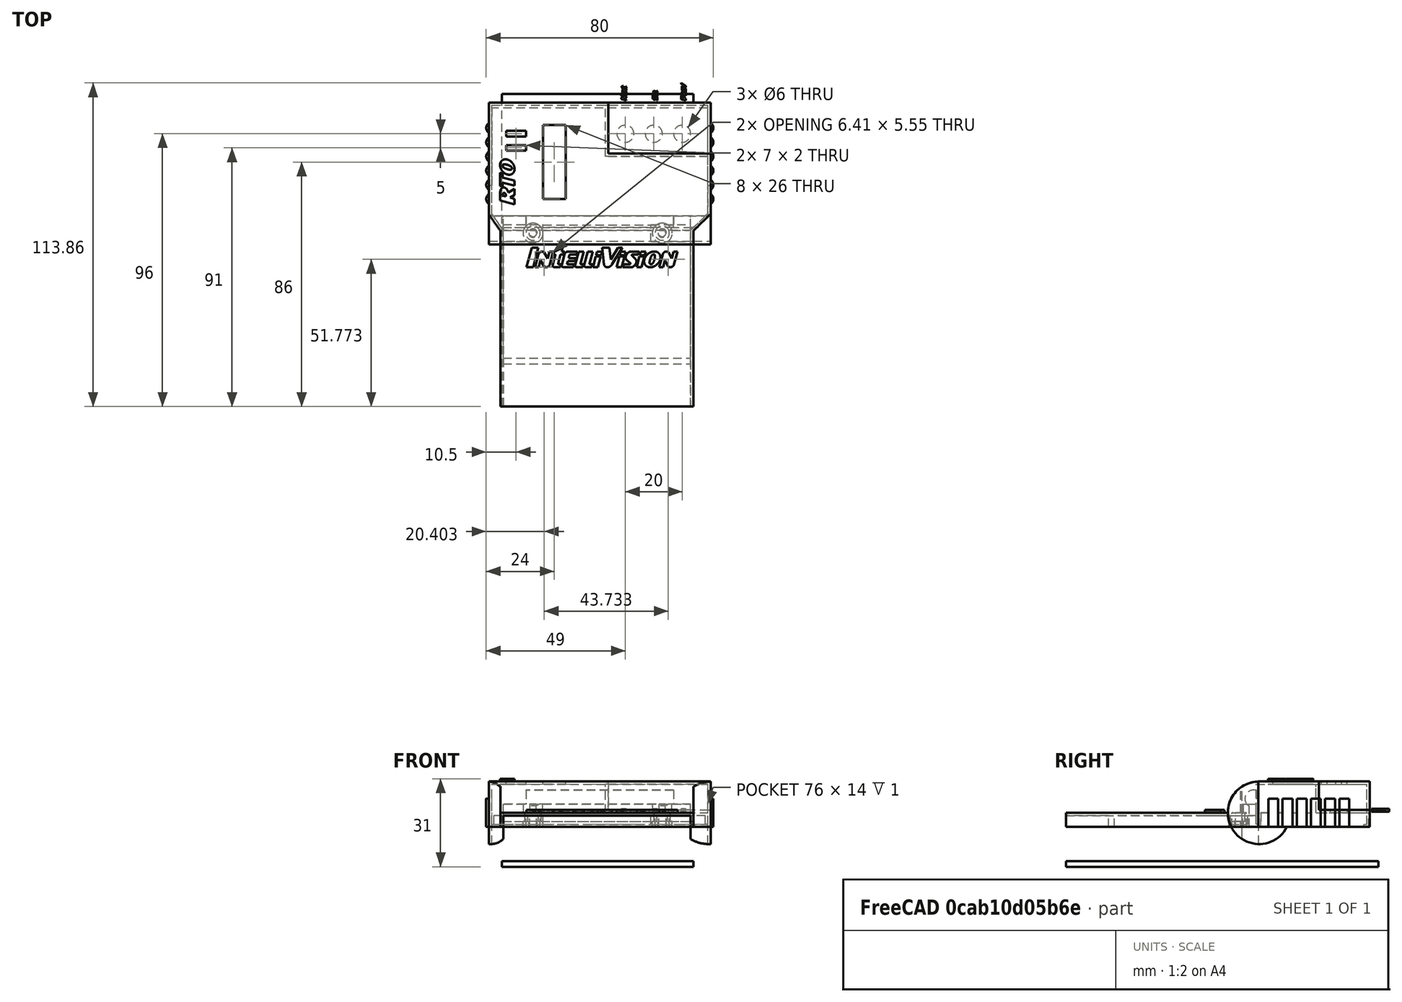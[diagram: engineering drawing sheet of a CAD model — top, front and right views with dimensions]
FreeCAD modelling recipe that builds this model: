
FCSTD DOCUMENT  (FreeCAD 0.20R29410 (Git))
Label: RTO11a_Cart_TOP
License: All rights reserved
LicenseURL: http://en.wikipedia.org/wiki/All_rights_reserved
objects: Part::Box×20, Part::Cut×19, Part::MultiFuse×18, Part::Cylinder×17, Part::Extrusion×6, Part::Part2DObjectPython×5, Part::FeaturePython×4, Part::Feature×4, Sketcher::SketchObject×3, PartDesign::Body×3, PartDesign::Pad×2, Part::Fillet×2, Mesh::Feature×2
note: 105 computed .brp shape members not serialized (recipe doc carries the construction recipe); baked Part::Feature solids carry a one-line shape summary decoded from their .brp

FEATURE [Sketcher::SketchObject] Sketch
  FullyConstrained = true
  MapMode = 5
  Support = -> [XY_Plane009]
  sketch-geometry (4):
    g0: LineSegment StartX=-67.5 StartY=110 StartZ=0 EndX=0 EndY=110 EndZ=0
    g1: LineSegment StartX=0 StartY=110 StartZ=0 EndX=0 EndY=0 EndZ=0
    g2: LineSegment StartX=0 StartY=0 StartZ=0 EndX=-67.5 EndY=0 EndZ=0
    g3: LineSegment StartX=-67.5 StartY=0 StartZ=0 EndX=-67.5 EndY=110 EndZ=0
  constraints (12):
    c: Coincident(g0,g1)
    c: Coincident(g1,g2)
    c: Coincident(g2,g3)
    c: Coincident(g3,g0)
    c: Horizontal(g0)
    c: Horizontal(g2)
    c: Vertical(g1)
    c: Vertical(g3)
    c: DistanceX(g0,g0) = 67.5
    c: DistanceY(g1,g1) = 110
    c: DistanceX(g-1,g1) = 0
    c: DistanceY(g1,g-1) = 0
FEATURE [PartDesign::Pad] Pad
  Direction = (0,0,1)
  Length = 2
  Length2 = 10
  Profile = -> Sketch
  ReferenceAxis = -> Sketch [N_Axis]
  Type = 0
FEATURE [PartDesign::Body] Body002  label="TOP"
  Origin = -> Origin002
  Placement = pos=(0,0,4) rot=(0,0,1;0rad)
FEATURE [PartDesign::Body] Body
  Group = -> [Sketch,Pad]
  Origin = -> Origin007
  Tip = -> Pad
FEATURE [Part::FeaturePython] Tube  # WARN: FeaturePython — macro-defined, semantics opaque (R4)
  AttacherType = Attacher::AttachEngine3D
  Height = 5
  InnerRadius = 1.25
  OuterRadius = 2.5
  Placement = pos=(-11,61,14) rot=(0,0,1;0rad)
FEATURE [Part::FeaturePython] Tube001  # WARN: FeaturePython — macro-defined, semantics opaque (R4)
  AttacherType = Attacher::AttachEngine3D
  Height = 5
  InnerRadius = 1.25
  OuterRadius = 2.5
  Placement = pos=(-56.5,61,14) rot=(0,0,1;0rad)
FEATURE [Part::Part2DObjectPython] ShapeString  # Draft 2D object (typed FeaturePython)
  FontFile = <userpath>/Documents/Retrocomputer/Intellivision/3DModel/sfintell.ttf
  MakeFace = true
  Size = 4
  String = IntelliVision
  Tracking = 0
FEATURE [Part::Extrusion] Extrude  label="Scritta"
  Base = -> ShapeString
  Dir = (0,0,1)
  DirMode = 2
  FaceMakerClass = Part::FaceMakerBullseye
  LengthFwd = 2
  LengthRev = 0
  Placement = pos=(-59,49,18) rot=(0,0,1;0rad)
  Solid = false
  Symmetric = false
FEATURE [Part::Box] Box  label="BasePillarSx"
  AttacherType = Attacher::AttachEngine3D
  Height = 3
  Length = 14
  Placement = pos=(-67,58,15) rot=(0,0,1;0rad)
  Width = 6
FEATURE [Part::Box] Box006  label="BasePillarDx"
  AttacherType = Attacher::AttachEngine3D
  Height = 3
  Length = 14
  Placement = pos=(-15,58,15) rot=(0,0,1;0rad)
  Width = 6
FEATURE [Sketcher::SketchObject] Sketch022
  AttachmentOffset = pos=(0,0,19) rot=(0,0,1;0rad)
  FullyConstrained = true
  MapMode = 5
  Placement = pos=(0,0,19) rot=(0,0,1;0rad)
  Support = -> [XY_Plane]
  sketch-geometry (8):
    g0: LineSegment StartX=0 StartY=0 StartZ=0 EndX=-68 EndY=0 EndZ=0
    g1: LineSegment StartX=-68 StartY=0 StartZ=0 EndX=-68 EndY=62 EndZ=0
    g2: LineSegment StartX=-68 StartY=62 StartZ=0 EndX=-72.0041 EndY=68.6121 EndZ=0
    g3: LineSegment StartX=-72.0041 StartY=68.6121 StartZ=0 EndX=-72.0041 EndY=106.612 EndZ=0
    g4: LineSegment StartX=-72.0041 StartY=106.612 StartZ=0 EndX=5.99595 EndY=106.612 EndZ=0
    g5: LineSegment StartX=5.99595 StartY=106.612 StartZ=0 EndX=5.99595 EndY=69.6121 EndZ=0
    g6: LineSegment StartX=5.99595 StartY=69.6121 StartZ=0 EndX=-9e-16 EndY=62 EndZ=0
    g7: LineSegment StartX=-9e-16 StartY=62 StartZ=0 EndX=0 EndY=0 EndZ=0
  constraints (24):
    c: PointOnObject(g0,g-2)
    c: PointOnObject(g0,g-1)
    c: Horizontal(g0)
    c: Coincident(g0,g1)
    c: Vertical(g1)
    c: Coincident(g1,g2)
    c: Coincident(g2,g3)
    c: Vertical(g3)
    c: Coincident(g3,g4)
    c: Horizontal(g4)
    c: Coincident(g4,g5)
    c: Vertical(g5)
    c: Coincident(g5,g6)
    c: PointOnObject(g6,g-2)
    c: Coincident(g6,g7)
    c: DistanceY(g1,g1) = 62
    c: DistanceY(g7,g7) = 62
    c: Coincident(g0,g7)
    c: DistanceX(g4,g4) = 78
    c: DistanceX(g0,g0) = 68
    c: DistanceY(g3,g3) = 38
    c: DistanceY(g5,g5) = 37
    c: Distance(g6) = 9.69
    c: Distance(g2) = 7.73
FEATURE [Part::Extrusion] Extrude001  label="BaseEsterna"
  Base = -> Sketch022
  Dir = (0,0,1)
  DirMode = 2
  FaceMakerClass = Part::FaceMakerBullseye
  LengthFwd = 5
  LengthRev = 0
  Reversed = true
  Solid = true
  Symmetric = false
FEATURE [Sketcher::SketchObject] Sketch005
  AttachmentOffset = pos=(-1,0,3) rot=(0,0,1;0rad)
  FullyConstrained = true
  MapMode = 5
  Placement = pos=(-1,0,3) rot=(0,0,1;0rad)
  Support = -> [XY_Plane010]
  sketch-geometry (8):
    g0: LineSegment StartX=0 StartY=0 StartZ=0 EndX=-66 EndY=0 EndZ=0
    g1: LineSegment StartX=-66 StartY=0 StartZ=0 EndX=-66 EndY=62 EndZ=0
    g2: LineSegment StartX=-66 StartY=62 StartZ=0 EndX=-70 EndY=67.82 EndZ=0
    g3: LineSegment StartX=-70 StartY=67.82 StartZ=0 EndX=-70 EndY=105 EndZ=0
    g4: LineSegment StartX=-70 StartY=105 StartZ=0 EndX=6 EndY=105 EndZ=0
    g5: LineSegment StartX=6 StartY=105 StartZ=0 EndX=6 EndY=67.82 EndZ=0
    g6: LineSegment StartX=6 StartY=67.82 StartZ=0 EndX=0 EndY=62 EndZ=0
    g7: LineSegment StartX=0 StartY=62 StartZ=0 EndX=0 EndY=0 EndZ=0
  constraints (24):
    c: PointOnObject(g0,g-2)
    c: PointOnObject(g0,g-1)
    c: Horizontal(g0)
    c: Coincident(g0,g1)
    c: Vertical(g1)
    c: Coincident(g1,g2)
    c: Coincident(g2,g3)
    c: Vertical(g3)
    c: Coincident(g3,g4)
    c: Horizontal(g4)
    c: Coincident(g4,g5)
    c: Vertical(g5)
    c: Coincident(g5,g6)
    c: PointOnObject(g6,g-2)
    c: Coincident(g6,g7)
    c: DistanceY(g1,g1) = 62
    c: DistanceY(g7,g7) = 62
    c: Coincident(g0,g7)
    c: DistanceX(g4,g4) = 76
    c: DistanceX(g0,g0) = 66
    c: Distance(g1,g4) = 43
    c: DistanceX(g2,g1) = 4
    c: DistanceY(g5,g2) = 0
    c: DistanceY(g6,g5) = 5.82
FEATURE [PartDesign::Pad] Pad001
  Direction = (0,0,1)
  Length = 15
  Length2 = 10
  Profile = -> Sketch005
  ReferenceAxis = -> Sketch005 [N_Axis]
  Type = 0
FEATURE [PartDesign::Body] Body003  label="BaseInterna"
  Group = -> [Sketch005,Pad001]
  Origin = -> Origin
  Tip = -> Pad001
FEATURE [Part::Box] Box007  label="Cubo"
  AttacherType = Attacher::AttachEngine3D
  Height = 16
  Length = 78
  Placement = pos=(-72,68,14) rot=(0,0,1;0rad)
  Width = 39
FEATURE [Part::Cylinder] Cylinder  label="Cilindro"
  Angle = 360
  AttacherType = Attacher::AttachEngine3D
  FirstAngle = 0
  Height = 78
  Placement = pos=(6,68,19) rot=(0,-1,0;1.5708rad)
  Radius = 11
  SecondAngle = 0
FEATURE [Part::MultiFuse] Fusion
  Shapes = -> [Extrude001,Box007,Cylinder]
FEATURE [Part::Box] Box008  label="Cubo001"
  AttacherType = Attacher::AttachEngine3D
  Height = 14
  Length = 76
  Placement = pos=(-71,67,15) rot=(0,0,1;0rad)
  Width = 39
FEATURE [Part::Box] Box009  label="Cubo002"
  AttacherType = Attacher::AttachEngine3D
  Height = 10
  Length = 66
  Placement = pos=(-67,62,12) rot=(0,0,1;0rad)
  Width = 6
FEATURE [Part::Cylinder] Cylinder006  label="Cilindro006"
  Angle = 360
  AttacherType = Attacher::AttachEngine3D
  FirstAngle = 0
  Height = 10
  Placement = pos=(5,78,1) rot=(0,0,1;0rad)
  Radius = 2
  SecondAngle = 0
FEATURE [Part::Cylinder] Cylinder007  label="Cilindro007"
  Angle = 360
  AttacherType = Attacher::AttachEngine3D
  FirstAngle = 0
  Height = 10
  Placement = pos=(5,73,1) rot=(0,0,1;0rad)
  Radius = 2
  SecondAngle = 0
FEATURE [Part::Cylinder] Cylinder008  label="Cilindro008"
  Angle = 360
  AttacherType = Attacher::AttachEngine3D
  FirstAngle = 0
  Height = 10
  Placement = pos=(5,83,1) rot=(0,0,1;0rad)
  Radius = 2
  SecondAngle = 0
FEATURE [Part::Cylinder] Cylinder009  label="Cilindro009"
  Angle = 360
  AttacherType = Attacher::AttachEngine3D
  FirstAngle = 0
  Height = 10
  Placement = pos=(5,88,1) rot=(0,0,1;0rad)
  Radius = 2
  SecondAngle = 0
FEATURE [Part::Cylinder] Cylinder010  label="Cilindro010"
  Angle = 360
  AttacherType = Attacher::AttachEngine3D
  FirstAngle = 0
  Height = 10
  Placement = pos=(5,93,1) rot=(0,0,1;0rad)
  Radius = 2
  SecondAngle = 0
FEATURE [Part::Cylinder] Cylinder011  label="Cilindro011"
  Angle = 360
  AttacherType = Attacher::AttachEngine3D
  FirstAngle = 0
  Height = 10
  Placement = pos=(5,98,1) rot=(0,0,1;0rad)
  Radius = 2
  SecondAngle = 0
FEATURE [Part::MultiFuse] Fusion009  label="cil_rx"
  Placement = pos=(0,0,13) rot=(0,0,1;0rad)
  Shapes = -> [Cylinder006,Cylinder007,Cylinder008,Cylinder009,Cylinder010,Cylinder011]
FEATURE [Part::Cylinder] Cylinder012  label="Cilindro012"
  Angle = 360
  AttacherType = Attacher::AttachEngine3D
  FirstAngle = 0
  Height = 10
  Placement = pos=(5,78,1) rot=(0,0,1;0rad)
  Radius = 2
  SecondAngle = 0
FEATURE [Part::Cylinder] Cylinder013  label="Cilindro013"
  Angle = 360
  AttacherType = Attacher::AttachEngine3D
  FirstAngle = 0
  Height = 10
  Placement = pos=(5,73,1) rot=(0,0,1;0rad)
  Radius = 2
  SecondAngle = 0
FEATURE [Part::Cylinder] Cylinder014  label="Cilindro014"
  Angle = 360
  AttacherType = Attacher::AttachEngine3D
  FirstAngle = 0
  Height = 10
  Placement = pos=(5,83,1) rot=(0,0,1;0rad)
  Radius = 2
  SecondAngle = 0
FEATURE [Part::Cylinder] Cylinder015  label="Cilindro015"
  Angle = 360
  AttacherType = Attacher::AttachEngine3D
  FirstAngle = 0
  Height = 10
  Placement = pos=(5,88,1) rot=(0,0,1;0rad)
  Radius = 2
  SecondAngle = 0
FEATURE [Part::Cylinder] Cylinder016  label="Cilindro016"
  Angle = 360
  AttacherType = Attacher::AttachEngine3D
  FirstAngle = 0
  Height = 10
  Placement = pos=(5,93,1) rot=(0,0,1;0rad)
  Radius = 2
  SecondAngle = 0
FEATURE [Part::Cylinder] Cylinder017  label="Cilindro017"
  Angle = 360
  AttacherType = Attacher::AttachEngine3D
  FirstAngle = 0
  Height = 10
  Placement = pos=(5,98,1) rot=(0,0,1;0rad)
  Radius = 2
  SecondAngle = 0
FEATURE [Part::MultiFuse] Fusion010  label="cil_dx"
  Placement = pos=(-76,0,13) rot=(0,0,1;0rad)
  Shapes = -> [Cylinder012,Cylinder013,Cylinder014,Cylinder015,Cylinder016,Cylinder017]
FEATURE [Part::MultiFuse] Fusion011
  Shapes = -> [Fusion,Fusion009,Fusion010]
FEATURE [Part::Cut] Cut
  Base = -> Fusion011
  Tool = -> Body003
FEATURE [Part::Cut] Cut001
  Base = -> Cut
  Tool = -> Box009
FEATURE [Part::Cylinder] Cylinder018  label="Bt3"
  Angle = 360
  AttacherType = Attacher::AttachEngine3D
  FirstAngle = 0
  Height = 10
  Placement = pos=(-4,96,16) rot=(0,0,1;0rad)
  Radius = 3
  SecondAngle = 0
FEATURE [Part::Cylinder] Cylinder019  label="Bt2"
  Angle = 360
  AttacherType = Attacher::AttachEngine3D
  FirstAngle = 0
  Height = 10
  Placement = pos=(-14,96,16) rot=(0,0,1;0rad)
  Radius = 3
  SecondAngle = 0
FEATURE [Part::Cylinder] Cylinder020  label="Bt1"
  Angle = 360
  AttacherType = Attacher::AttachEngine3D
  FirstAngle = 0
  Height = 10
  Placement = pos=(-24,96,16) rot=(0,0,1;0rad)
  Radius = 3
  SecondAngle = 0
FEATURE [Part::Box] Box010  label="Cubo003"
  AttacherType = Attacher::AttachEngine3D
  Height = 10
  Length = 8
  Placement = pos=(-53,73,22) rot=(0,0,1;0rad)
  Width = 26
FEATURE [Part::Box] Box011  label="Cubo004"
  AttacherType = Attacher::AttachEngine3D
  Height = 21
  Length = 11
  Placement = pos=(5,57,10) rot=(0,0,1;0.767945rad)
  Width = 7
FEATURE [Part::Box] Box012  label="Cubo005"
  AttacherType = Attacher::AttachEngine3D
  Height = 22
  Length = 8
  Placement = pos=(-75.7,65.86,10) rot=(0,0,-1;0.959931rad)
  Width = 4
FEATURE [Part::Box] Box013  label="Cubo006"
  AttacherType = Attacher::AttachEngine3D
  Height = 20
  Length = 93
  Placement = pos=(-80,49,-6) rot=(0,0,1;0rad)
  Width = 30
FEATURE [Part::MultiFuse] Fusion012
  Shapes = -> [Extrude]
FEATURE [Part::Part2DObjectPython] ShapeString001  # Draft 2D object (typed FeaturePython)
  FontFile = <userpath>/Documents/Retrocomputer/Intellivision/3DModel/sfintell.ttf
  MakeFace = true
  Placement = pos=(0,0,0) rot=(0,0,1;1.5708rad)
  Size = 3
  String = RTO
  Tracking = 0
FEATURE [Part::Extrusion] Extrude002  label="ScrittaRTO"
  Base = -> ShapeString001
  Dir = (0,0,1)
  DirMode = 2
  FaceMakerClass = Part::FaceMakerBullseye
  LengthFwd = 2
  LengthRev = 0
  Placement = pos=(-63,71,29) rot=(1,0,0;0rad)
  Solid = false
  Symmetric = false
FEATURE [Part::MultiFuse] Fusion013  label="Scritte"
  Shapes = -> [Fusion012,Extrude002]
FEATURE [Part::MultiFuse] Fusion014  label="FinaleTOP"
  Shapes = -> [Fusion013]
FEATURE [Part::Cut] Cut010
  Base = -> Cut001
  Tool = -> Box008
FEATURE [Part::Cut] Cut011
  Base = -> Cut010
  Tool = -> Box013
FEATURE [Part::Box] Box014  label="holdertop"
  AttacherType = Attacher::AttachEngine3D
  Height = 5
  Length = 66
  Placement = pos=(-67,15,14) rot=(0,0,1;0rad)
  Width = 2
FEATURE [Part::MultiFuse] Fusion016
  Shapes = -> [Fusion014]
FEATURE [Part::Box] Box015  label="BtnsPlace"
  AttacherType = Attacher::AttachEngine3D
  Height = 10
  Length = 38
  Placement = pos=(-30,89,20) rot=(0,0,1;0rad)
  Width = 18
FEATURE [Part::Cut] Cut015  label="Scritte001"
  Base = -> Fusion016
  Tool = -> Box015
FEATURE [Part::Box] Box016  label="Cubo009"
  AttacherType = Attacher::AttachEngine3D
  Height = 1
  Length = 35
  Placement = pos=(-30,89,19) rot=(0,0,1;0rad)
  Width = 18
FEATURE [Part::Box] Box017  label="Cubo010"
  AttacherType = Attacher::AttachEngine3D
  Height = 11
  Length = 35
  Placement = pos=(-30,88,19) rot=(0,0,1;0rad)
  Width = 1
FEATURE [Part::Box] Box018  label="Cubo011"
  AttacherType = Attacher::AttachEngine3D
  Height = 11
  Length = 1
  Placement = pos=(-31,88,19) rot=(0,0,1;0rad)
  Width = 18
FEATURE [Part::Box] Box019  label="Cubo012"
  AttacherType = Attacher::AttachEngine3D
  Height = 1
  Length = 1
  Placement = pos=(4,88,19) rot=(0,0,1;0rad)
  Width = 19
FEATURE [Part::MultiFuse] Fusion017  label="BtnBase"
  Shapes = -> [Box016,Box017,Box018,Box019]
FEATURE [Part::Box] Box020  label="Led1"
  AttacherType = Attacher::AttachEngine3D
  Height = 8
  Length = 7
  Placement = pos=(-66,90,24) rot=(0,0,1;0rad)
  Width = 2
FEATURE [Part::Box] Box021  label="Led2"
  AttacherType = Attacher::AttachEngine3D
  Height = 8
  Length = 7
  Placement = pos=(-66,95,24) rot=(0,0,1;0rad)
  Width = 2
FEATURE [Part::Cut] Cut016
  Base = -> Cut001
  Tool = -> Box008
FEATURE [Part::Box] Box022  label="Cubo013"
  AttacherType = Attacher::AttachEngine3D
  Height = 21
  Length = 10
  Placement = pos=(0,53,10) rot=(0,0,1;0rad)
  Width = 9
FEATURE [Part::Cut] Cut018
  Base = -> Cut011
  Tool = -> Box011
FEATURE [Part::Cut] Cut019
  Base = -> Cut018
  Tool = -> Box022
FEATURE [Part::Box] Box023  label="Cubo014"
  AttacherType = Attacher::AttachEngine3D
  Height = 21
  Length = 9
  Placement = pos=(-77,52,10) rot=(0,0,-1;0rad)
  Width = 9.5
FEATURE [Part::Cut] Cut020
  Base = -> Cut019
  Tool = -> Box012
FEATURE [Part::Cut] Cut021
  Base = -> Cut020
  Tool = -> Box023
FEATURE [Part::Cut] Cut022
  Base = -> Cut021
  Tool = -> Box015
FEATURE [Part::Cut] Cut023
  Base = -> Fusion017
  Tool = -> Cylinder020
FEATURE [Part::Cut] Cut024
  Base = -> Cut023
  Tool = -> Cylinder019
FEATURE [Part::Cut] Cut025
  Base = -> Cut024
  Tool = -> Cylinder018
FEATURE [Part::MultiFuse] Fusion018
  Shapes = -> [Cut022,Cut025]
FEATURE [Part::Cut] Cut026
  Base = -> Fusion018
  Tool = -> Box020
FEATURE [Part::Cut] Cut027
  Base = -> Cut026
  Tool = -> Box021
FEATURE [Part::Cut] Cut028
  Base = -> Cut027
  Tool = -> Box010
FEATURE [Part::MultiFuse] Fusion019
  Shapes = -> [Cut028,Box014]
FEATURE [Part::MultiFuse] Fusion020
  Shapes = -> [Cut015,Fusion019]
FEATURE [Part::Cut] Cut017
  Base = -> Cut010
  Tool = -> Box013
FEATURE [Part::Fillet] Fillet
  Base = -> Fusion020
  Edges = 1 edges r=0.7: [Edge255]
FEATURE [Part::Fillet] Fillet001  label="Final_Top"
  Base = -> Fillet
  Edges = 2 edges r=0.6: [Edge11,Edge13]
FEATURE [Part::Feature] Refined_Mesh_Solid_81622  label="Refined_Mesh_Bottom"
  Placement = pos=(0,0,3) rot=(0,0,1;0rad)
  shape: bbox 80 x 107 x 11 mm, 687 faces, 0 solids (baked)
FEATURE [Part::FeaturePython] Tube002  # WARN: FeaturePython — macro-defined, semantics opaque (R4)
  AttacherType = Attacher::AttachEngine3D
  Height = 8
  InnerRadius = 1.5
  OuterRadius = 3.5
  Placement = pos=(-11,61,14) rot=(0,0,1;0rad)
FEATURE [Part::FeaturePython] Tube003  # WARN: FeaturePython — macro-defined, semantics opaque (R4)
  AttacherType = Attacher::AttachEngine3D
  Height = 8
  InnerRadius = 1.5
  OuterRadius = 3.5
  Placement = pos=(-56.5,61,14) rot=(0,0,1;0rad)
FEATURE [Part::Part2DObjectPython] ShapeString002  # Draft 2D object (typed FeaturePython)
  FontFile = <userpath>/Documents/Retrocomputer/Intellivision/3DModel/sfintell.ttf
  MakeFace = true
  Placement = pos=(-23.69,99.6,20) rot=(0,0,1;1.5708rad)
  Size = 1
  String = Next
  Tracking = 0
FEATURE [Part::Extrusion] Extrude003  label="Next"
  Base = -> ShapeString002
  Dir = (0,0,1)
  DirMode = 2
  FaceMakerClass = Part::FaceMakerBullseye
  LengthFwd = 1
  LengthRev = 0
  Solid = false
  Symmetric = false
FEATURE [Part::Part2DObjectPython] ShapeString003  # Draft 2D object (typed FeaturePython)
  FontFile = <userpath>/Documents/Retrocomputer/Intellivision/3DModel/sfintell.ttf
  MakeFace = true
  Placement = pos=(-23.69,99.6,20) rot=(0,0,1;1.5708rad)
  Size = 1
  String = Sel
  Tracking = 0
FEATURE [Part::Extrusion] Extrude004  label="Sel"
  Base = -> ShapeString003
  Dir = (0,0,1)
  DirMode = 2
  FaceMakerClass = Part::FaceMakerBullseye
  LengthFwd = 1
  LengthRev = 0
  Placement = pos=(11,0,0) rot=(0,0,1;0rad)
  Solid = false
  Symmetric = false
FEATURE [Part::Part2DObjectPython] ShapeString004  # Draft 2D object (typed FeaturePython)
  FontFile = <userpath>/Documents/Retrocomputer/Intellivision/3DModel/sfintell.ttf
  MakeFace = true
  Placement = pos=(-23.69,99.6,20) rot=(0,0,1;1.5708rad)
  Size = 1
  String = Prev
  Tracking = 0
FEATURE [Part::Extrusion] Extrude005  label="Prev"
  Base = -> ShapeString004
  Dir = (0,0,1)
  DirMode = 2
  FaceMakerClass = Part::FaceMakerBullseye
  LengthFwd = 1
  LengthRev = 0
  Placement = pos=(21,0,0) rot=(0,0,1;0rad)
  Solid = false
  Symmetric = false
FEATURE [Part::MultiFuse] Fusion021
  Shapes = -> [Extrude003,Extrude004]
FEATURE [Part::MultiFuse] Fusion022  label="Btn_text"
  Placement = pos=(0,8,-0.6) rot=(0,0,1;0rad)
  Shapes = -> [Fusion021,Extrude005]
FEATURE [Part::MultiFuse] Fusion023
  Shapes = -> [Fillet001,Tube002]
FEATURE [Part::MultiFuse] Fusion024  label="TOP_Final"
  Shapes = -> [Fusion023,Tube003]
FEATURE [Mesh::Feature] Mesh  label="Btn_text (Meshed)"
FEATURE [Part::Feature] Refined_Mesh001_Solid_49575  label="Top_final_solid"
  shape: bbox 80 x 107 x 20 mm, 1586 faces, 0 solids (baked)
FEATURE [Part::Feature] Refined_Mesh_Solid_30061
  shape: bbox 22.71 x 6.206 x 1 mm, 400 faces, 0 solids (baked)
FEATURE [Part::MultiFuse] Fusion025
  Shapes = -> [Refined_Mesh_Solid_30061,Refined_Mesh001_Solid_49575]
FEATURE [Part::Cylinder] Cylinder021  label="Cilindro018"
  Angle = 360
  AttacherType = Attacher::AttachEngine3D
  FirstAngle = 0
  Height = 52
  Placement = pos=(-59,66,24) rot=(0,1,0;1.5708rad)
  Radius = 3
  SecondAngle = 0
FEATURE [Part::Cut] Cut029
  Base = -> Fusion024
  Tool = -> Cylinder021
FEATURE [Part::Box] Box024  label="Cubo015"
  AttacherType = Attacher::AttachEngine3D
  Height = 3
  Length = 68
  Placement = pos=(-68,58,16) rot=(0,0,1;0rad)
  Width = 5
FEATURE [Part::MultiFuse] Fusion026
  Shapes = -> [Cut029,Box024]
FEATURE [Mesh::Feature] Mesh001  label="Fusion026 (Meshed)"
FEATURE [Part::Feature] Refined_Mesh001_Solid_35499
  shape: bbox 80 x 107 x 17 mm, 1638 faces, 0 solids (baked)
